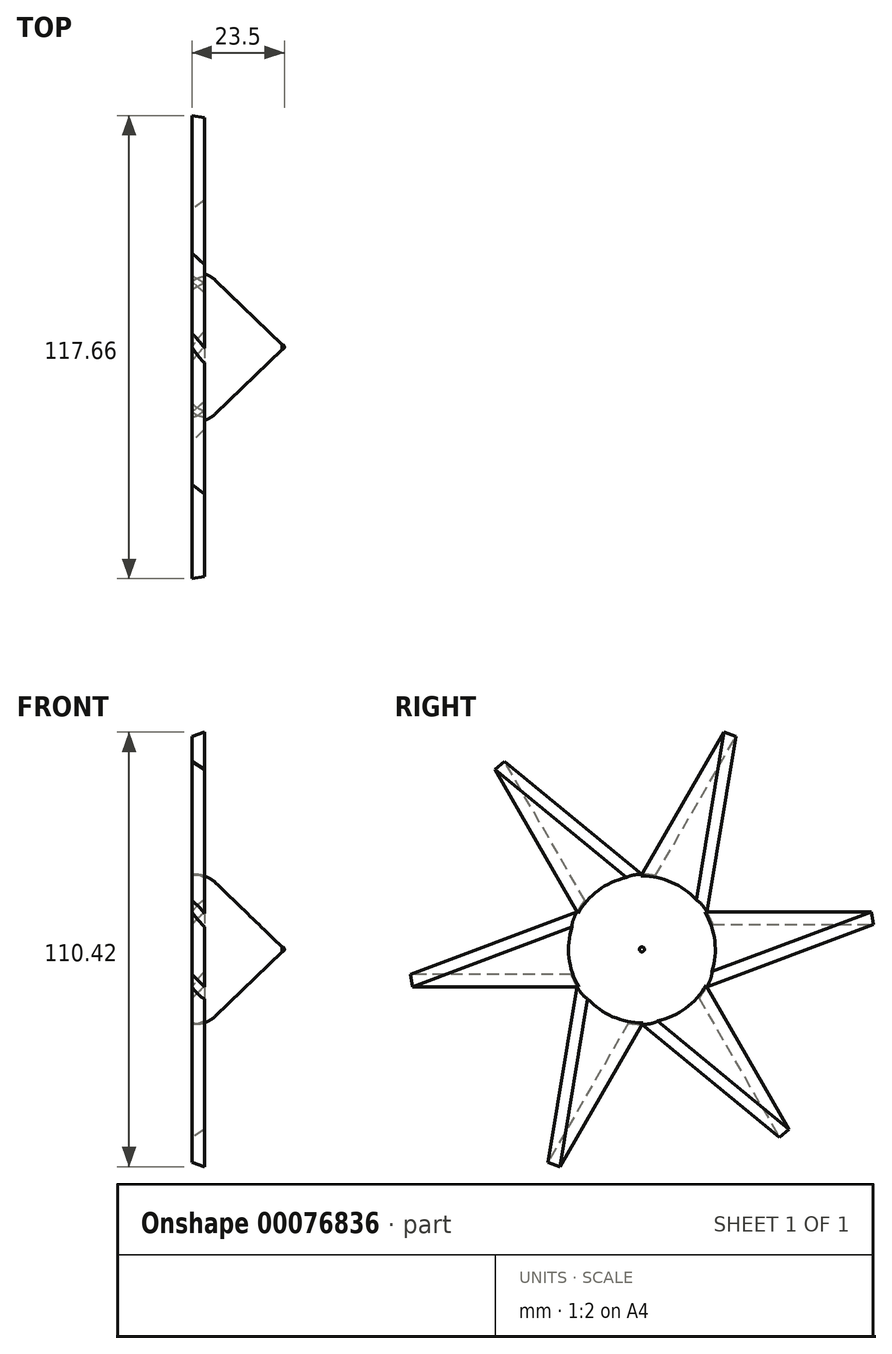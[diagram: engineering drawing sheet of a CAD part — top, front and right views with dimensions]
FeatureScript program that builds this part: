
annotation { "Feature Type Name" : "Feature", "Feature Type Description" : "" }
export const myFeature = defineFeature(function(context is Context, id is Id, definition is map)
    precondition{}
    {
        {
            var Q0;
            Q0=qCreatedBy(makeId("Right.planeOp"),FACE);
            var sketch = newSketch(context, id + "F0", { "sketchPlane" : qUnion([Q0])});
            skCircle(sketch, "E0", {"center": v(-67.13, 3.01) * mm, "radius": 19.05 * mm});
            skCircle(sketch, "E1.cCircle", {"center": v(-67.13, 3.01) * mm, "radius": 19.05 * mm, "construction": true});
            skLineSegment(sketch, "E2", {"start": v(-67.13, 22.06) * mm, "end": v(-43.48, 63.02) * mm});
            skLineSegment(sketch, "E3", {"start": v(-83.63, 12.54) * mm, "end": v(-107.28, 53.5) * mm});
            skLineSegment(sketch, "E4", {"start": v(-83.63, -6.51) * mm, "end": v(-130.93, -6.51) * mm});
            skLineSegment(sketch, "E5", {"start": v(-67.13, -16.04) * mm, "end": v(-90.78, -57) * mm});
            skLineSegment(sketch, "E6", {"start": v(-50.63, -6.51) * mm, "end": v(-26.98, -47.48) * mm});
            skLineSegment(sketch, "E7", {"start": v(-50.63, 12.54) * mm, "end": v(-3.33, 12.54) * mm});
            skLineSegment(sketch, "E8", {"start": v(-131.15, -5.28) * mm, "end": v(-83.63, 12.54) * mm});
            skLineSegment(sketch, "E9", {"start": v(-106.34, 54.31) * mm, "end": v(-67.13, 22.06) * mm});
            skLineSegment(sketch, "E10", {"start": v(-91.96, -56.58) * mm, "end": v(-83.63, -6.51) * mm});
            skLineSegment(sketch, "E11", {"start": v(-27.94, -48.28) * mm, "end": v(-67.13, -16.04) * mm});
            skLineSegment(sketch, "E12", {"start": v(-3.11, 11.3) * mm, "end": v(-50.63, -6.51) * mm});
            skLineSegment(sketch, "E13", {"start": v(-42.3, 62.6) * mm, "end": v(-50.63, 12.54) * mm});
            skPoint(sketch, "E14.visualSharp", {"position": v(-41.73, 66.06) * mm});
            skPoint(sketch, "E15.visualSharp", {"position": v(-109.03, 56.53) * mm});
            skPoint(sketch, "E16.visualSharp", {"position": v(-134.43, -6.51) * mm});
            skPoint(sketch, "E17.visualSharp", {"position": v(-92.53, -60.03) * mm});
            skPoint(sketch, "E18.visualSharp", {"position": v(-25.23, -50.5) * mm});
            skPoint(sketch, "E19.visualSharp", {"position": v(0.17, 12.54) * mm});
            skLineSegment(sketch, "E20", {"start": v(-107.28, 53.5) * mm, "end": v(-106.34, 54.31) * mm});
            skLineSegment(sketch, "E21", {"start": v(-43.48, 63.02) * mm, "end": v(-42.3, 62.6) * mm});
            skLineSegment(sketch, "E22", {"start": v(-3.33, 12.54) * mm, "end": v(-3.11, 11.3) * mm});
            skLineSegment(sketch, "E23", {"start": v(-27.94, -48.28) * mm, "end": v(-26.98, -47.48) * mm});
            skLineSegment(sketch, "E24", {"start": v(-90.78, -57) * mm, "end": v(-91.96, -56.58) * mm});
            skLineSegment(sketch, "E25", {"start": v(-130.93, -6.51) * mm, "end": v(-131.15, -5.28) * mm});
            skSolve(sketch);
        }
        {
            var Q0;
            {var subQ2=sQuery(id+"F0.wireOp",EDGE,"E4");Q0=makeQuery(id+"F0.imprint","IMPRINT",FACE,{"disambiguationData":[TD([[makeQuery(id+"F0.imprint","IMPRINT",EDGE,{"derivedFrom":subQ2}),-1.0]])]});}
            var Q1;
            {var subQ0=sQuery(id+"F0.wireOp",EDGE,"E0");var subQ4=makeQuery(id+"F0.imprint","INTERSECT",VERTEX,{"derivedFrom":[subQ0,sQuery(id+"F0.wireOp",EDGE,"E2"),sQuery(id+"F0.wireOp",EDGE,"E9")]});Q1=makeQuery(id+"F0.imprint","IMPRINT",FACE,{"disambiguationData":[TD([[makeQuery(id+"F0.imprint","IMPRINT",EDGE,{"disambiguationData":[TD([[subQ4,1.0]])],"derivedFrom":subQ0}),1.0]])]});}
            var Q2;
            {var subQ2=sQuery(id+"F0.wireOp",EDGE,"E3");Q2=makeQuery(id+"F0.imprint","IMPRINT",FACE,{"disambiguationData":[TD([[makeQuery(id+"F0.imprint","IMPRINT",EDGE,{"derivedFrom":subQ2}),-1.0]])]});}
            var Q3;
            {var subQ0=sQuery(id+"F0.wireOp",EDGE,"E2");Q3=makeQuery(id+"F0.imprint","IMPRINT",FACE,{"disambiguationData":[TD([[makeQuery(id+"F0.imprint","IMPRINT",EDGE,{"derivedFrom":subQ0}),-1.0]])]});}
            var Q4;
            {var subQ2=sQuery(id+"F0.wireOp",EDGE,"E5");Q4=makeQuery(id+"F0.imprint","IMPRINT",FACE,{"disambiguationData":[TD([[makeQuery(id+"F0.imprint","IMPRINT",EDGE,{"derivedFrom":subQ2}),-1.0]])]});}
            var Q5;
            {var subQ2=sQuery(id+"F0.wireOp",EDGE,"E6");Q5=makeQuery(id+"F0.imprint","IMPRINT",FACE,{"disambiguationData":[TD([[makeQuery(id+"F0.imprint","IMPRINT",EDGE,{"derivedFrom":subQ2}),-1.0]])]});}
            var Q6;
            {var subQ2=sQuery(id+"F0.wireOp",EDGE,"E7");Q6=makeQuery(id+"F0.imprint","IMPRINT",FACE,{"disambiguationData":[TD([[makeQuery(id+"F0.imprint","IMPRINT",EDGE,{"derivedFrom":subQ2}),-1.0]])]});}
            extrude(context, id + "F1", {"entities" : qUnion([Q0, Q1, Q2, Q3, Q4, Q5, Q6]), "depth" : 3.17 * mm});
        }
        {
            var Q0;
            {var subQ0=sQuery(id+"F0.wireOp",EDGE,"E0");var subQ4=makeQuery(id+"F0.imprint","INTERSECT",VERTEX,{"derivedFrom":[subQ0,sQuery(id+"F0.wireOp",EDGE,"E2"),sQuery(id+"F0.wireOp",EDGE,"E9")]});Q0=makeQuery(id+"F0.imprint","IMPRINT",FACE,{"disambiguationData":[TD([[makeQuery(id+"F0.imprint","IMPRINT",EDGE,{"disambiguationData":[TD([[subQ4,1.0]])],"derivedFrom":subQ0}),1.0]])]});}
            extrude(context, id + "F2", {"entities" : qUnion([Q0]), "operationType" : NewBodyOperationType.ADD, "depth" : 3.8 * mm});
        }
        {
            var Q0;
            Q0=makeQuery(id+"F2.opExtrude","CAP_FACE",FACE,{"disambiguationData":[OSD([sQuery(id+"F0.wireOp",EDGE,"E0")])],"isStart":false});
            cPlane(context, id + "F3", {"entities" : qUnion([Q0]), "cplaneType" : CPlaneType.OFFSET, "offset" : 19.05 * mm, "width" : 152.4 * mm, "height" : 152.4 * mm});
        }
        {
            var Q0;
            Q0=qCreatedBy(id+"F3.planeOp",FACE);
            var sketch = newSketch(context, id + "F4", { "sketchPlane" : qUnion([Q0])});
            skPoint(sketch, "E26", {"position": v(-67.13, 3.01) * mm});
            skCircle(sketch, "E27", {"center": v(-67.13, 3.01) * mm, "radius": 0.64 * mm});
            skLineSegment(sketch, "E28", {"start": v(-67.13, 3.01) * mm, "end": v(-67.13, 3.65) * mm});
            skLineSegment(sketch, "E29", {"start": v(-67.13, 3.65) * mm, "end": v(-67.13, 2.38) * mm});
            skSolve(sketch);
        }
        {
            var Q0;
            {var subQ0=sQuery(id+"F4.wireOp",EDGE,"E29");var subQ4=makeQuery(id+"F4.imprint","IMPRINT",VERTEX,{"derivedFrom":subQ0});Q0=makeQuery(id+"F4.imprint","IMPRINT",FACE,{"disambiguationData":[TD([[makeQuery(id+"F4.imprint","IMPRINT",EDGE,{"disambiguationData":[TD([[subQ4,1.0]])],"derivedFrom":subQ0}),1.0]])]});}
            var Q1;
            Q1=sQuery(id+"F4.wireOp",EDGE,"E29");
            revolve(context, id + "F5", {"entities" : qUnion([Q0]), "axis" : qUnion([Q1]), "revolveType" : RevolveType.ONE_DIRECTION, "angle" : 180 * degree});
        }
        {
            var Q0;
            Q0=makeQuery(id+"F2.opExtrude","CAP_FACE",FACE,{"disambiguationData":[OSD([sQuery(id+"F0.wireOp",EDGE,"E0")])],"isStart":false});
            var Q1;
            Q1=makeQuery(id+"F5.opRevolve","CAP_FACE",FACE,{"disambiguationData":[OSD([sQuery(id+"F4.wireOp",EDGE,"E27"),sQuery(id+"F4.wireOp",EDGE,"E29")])],"isStart":true});
            loft(context, id + "F6", {"operationType" : NewBodyOperationType.ADD, "sheetProfilesArray" : [{ "sheetProfileEntities" : qUnion([Q0]) }, { "sheetProfileEntities" : qUnion([Q1]) }]});
        }
        {
            var Q0;
            Q0=makeQuery(id+"F1.opExtrude","CAP_EDGE",EDGE,{"disambiguationData":[OSD([sQuery(id+"F0.wireOp",EDGE,"E12")])],"isStart":false});
            var Q1;
            Q1=makeQuery(id+"F1.opExtrude","CAP_EDGE",EDGE,{"disambiguationData":[OSD([sQuery(id+"F0.wireOp",EDGE,"E11")])],"isStart":false});
            var Q2;
            Q2=makeQuery(id+"F1.opExtrude","CAP_EDGE",EDGE,{"disambiguationData":[OSD([sQuery(id+"F0.wireOp",EDGE,"E10")])],"isStart":false});
            var Q3;
            Q3=makeQuery(id+"F1.opExtrude","CAP_EDGE",EDGE,{"disambiguationData":[OSD([sQuery(id+"F0.wireOp",EDGE,"E8")])],"isStart":false});
            var Q4;
            Q4=makeQuery(id+"F1.opExtrude","CAP_EDGE",EDGE,{"disambiguationData":[OSD([sQuery(id+"F0.wireOp",EDGE,"E9")])],"isStart":false});
            var Q5;
            Q5=makeQuery(id+"F1.opExtrude","CAP_EDGE",EDGE,{"disambiguationData":[OSD([sQuery(id+"F0.wireOp",EDGE,"E13")])],"isStart":false});
            chamfer(context, id + "F7", {"entities" : qUnion([Q0, Q1, Q2, Q3, Q4, Q5]), "width" : 3.17 * mm, "tangentPropagation" : true});
        }
        {
            var Q0;
            Q0=makeQuery(id+"F1.opExtrude","CAP_EDGE",EDGE,{"disambiguationData":[OSD([sQuery(id+"F0.wireOp",EDGE,"E3")])],"isStart":true});
            var Q1;
            Q1=makeQuery(id+"F1.opExtrude","CAP_EDGE",EDGE,{"disambiguationData":[OSD([sQuery(id+"F0.wireOp",EDGE,"E4")])],"isStart":true});
            var Q2;
            Q2=makeQuery(id+"F1.opExtrude","CAP_EDGE",EDGE,{"disambiguationData":[OSD([sQuery(id+"F0.wireOp",EDGE,"E5")])],"isStart":true});
            var Q3;
            Q3=makeQuery(id+"F1.opExtrude","CAP_EDGE",EDGE,{"disambiguationData":[OSD([sQuery(id+"F0.wireOp",EDGE,"E6")])],"isStart":true});
            var Q4;
            Q4=makeQuery(id+"F1.opExtrude","CAP_EDGE",EDGE,{"disambiguationData":[OSD([sQuery(id+"F0.wireOp",EDGE,"E7")])],"isStart":true});
            var Q5;
            Q5=makeQuery(id+"F1.opExtrude","CAP_EDGE",EDGE,{"disambiguationData":[OSD([sQuery(id+"F0.wireOp",EDGE,"E2")])],"isStart":true});
            chamfer(context, id + "F8", {"entities" : qUnion([Q0, Q1, Q2, Q3, Q4, Q5]), "width" : 3.17 * mm, "tangentPropagation" : true});
        }
        {
            var Q0;
            {var subQ0=sQuery(id+"F0.wireOp",EDGE,"E0");Q0=makeQuery(id+"F6.boolean.opBoolean","MERGE",EDGE,{"derivedFrom":[makeQuery(id+"F2.opExtrude","CAP_EDGE",EDGE,{"disambiguationData":[OSD([subQ0])],"isStart":false}),makeQuery(id+"F6.opLoft","MID_CAP_EDGE",EDGE,{"disambiguationData":[OSD([subQ0])],"capPos":0.0})]});}
            fillet(context, id + "F9", {"entities" : qUnion([Q0]), "radius" : 7.62 * mm, "tangentPropagation" : true, "allowEdgeOverflow" : false});
        }
    });
